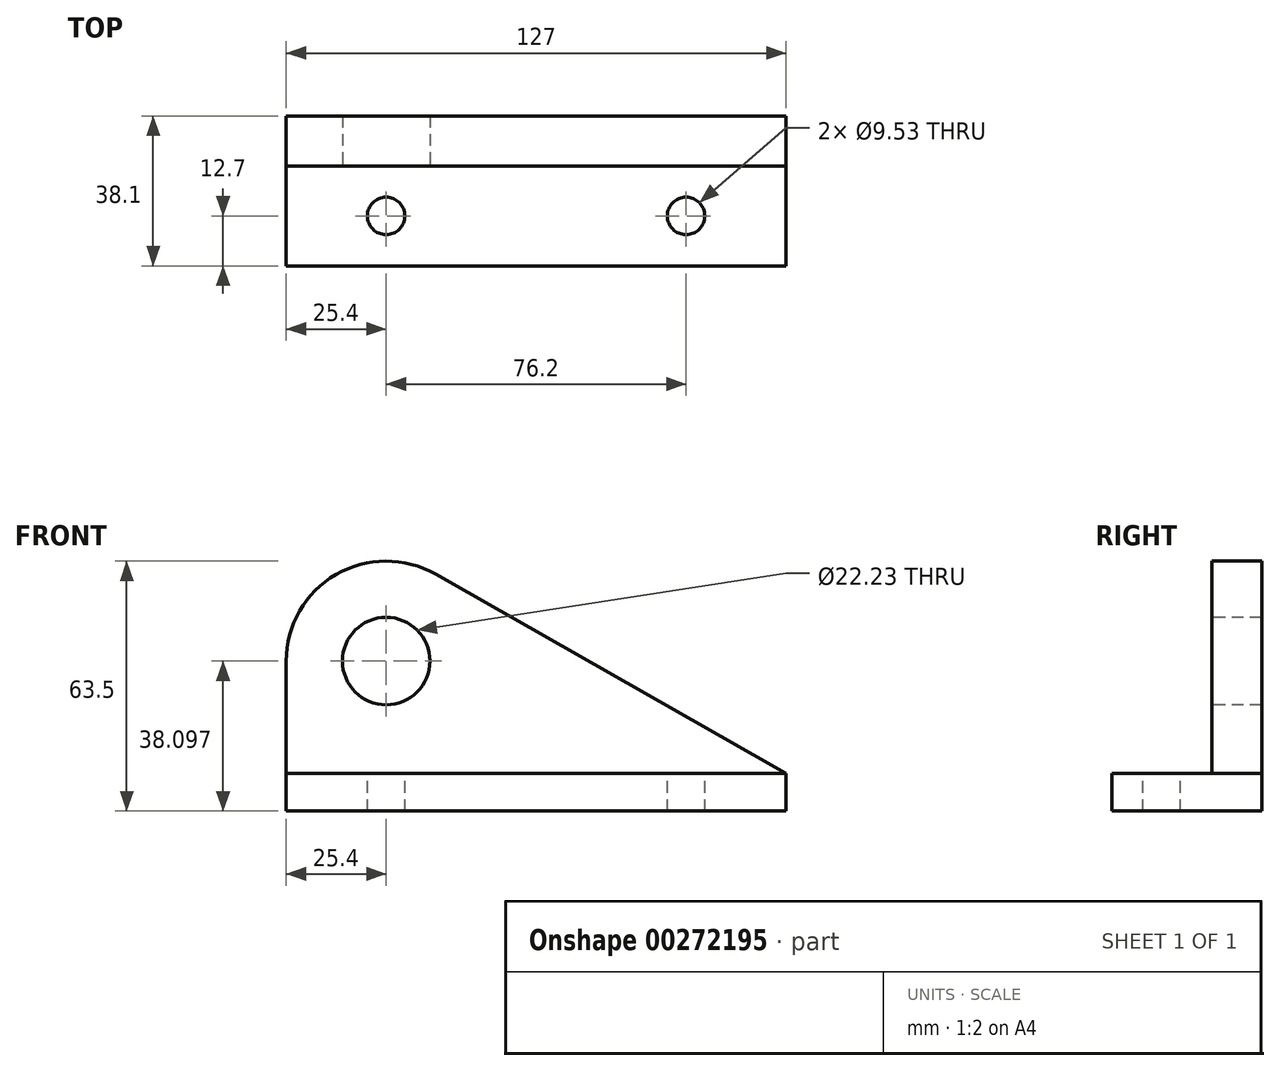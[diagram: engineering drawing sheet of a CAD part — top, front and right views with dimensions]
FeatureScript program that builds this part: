
annotation { "Feature Type Name" : "Feature", "Feature Type Description" : "" }
export const myFeature = defineFeature(function(context is Context, id is Id, definition is map)
    precondition{}
    {
        {
            var Q0;
            Q0=qCreatedBy(makeId("Front.planeOp"),FACE);
            var sketch = newSketch(context, id + "F0", { "sketchPlane" : qUnion([Q0])});
            skLineSegment(sketch, "E0.bottom", {"start": v(-63.5, 4.76) * mm, "end": v(63.5, 4.76) * mm});
            skLineSegment(sketch, "E0.top", {"start": v(-63.5, -4.76) * mm, "end": v(63.5, -4.76) * mm});
            skLineSegment(sketch, "E0.left", {"start": v(-63.5, 4.76) * mm, "end": v(-63.5, -4.76) * mm});
            skLineSegment(sketch, "E0.right", {"start": v(63.5, 4.76) * mm, "end": v(63.5, -4.76) * mm});
            skPoint(sketch, "E0.middle", {"position": v(0, 0) * mm});
            skSolve(sketch);
        }
        {
            var Q0;
            Q0=makeQuery(id+"F0.imprint","IMPRINT",FACE,{"disambiguationData":[TD([[makeQuery(id+"F0.imprint","IMPRINT",EDGE,{"derivedFrom":sQuery(id+"F0.wireOp",EDGE,"E0.bottom")}),-1.0]])]});
            extrude(context, id + "F1", {"entities" : qUnion([Q0]), "endBound" : BoundingType.SYMMETRIC, "depth" : 38.1 * mm});
        }
        {
            var Q0;
            Q0=makeQuery(id+"F1.opExtrude","CAP_FACE",FACE,{"disambiguationData":[OSD([sQuery(id+"F0.wireOp",EDGE,"E0.bottom"),sQuery(id+"F0.wireOp",EDGE,"E0.top"),sQuery(id+"F0.wireOp",EDGE,"E0.left"),sQuery(id+"F0.wireOp",EDGE,"E0.right")])],"isStart":true});
            var sketch = newSketch(context, id + "F2", { "sketchPlane" : qUnion([Q0])});
            skLineSegment(sketch, "E1", {"start": v(63.5, 4.76) * mm, "end": v(38.1, 4.76) * mm});
            skLineSegment(sketch, "E2", {"start": v(31.88, 70.41) * mm, "end": v(36.21, 70.41) * mm});
            skLineSegment(sketch, "E3", {"start": v(38.1, 4.76) * mm, "end": v(38.1, 33.34) * mm});
            skArc(sketch, "E4", {"start": v(63.5, 33.34) * mm, "mid": v(50.87, 55.3) * mm, "end": v(25.54, 55.42) * mm});
            skLineSegment(sketch, "E5", {"start": v(63.5, 4.76) * mm, "end": v(63.5, 33.34) * mm});
            skLineSegment(sketch, "E6", {"start": v(-63.5, 4.76) * mm, "end": v(25.54, 55.42) * mm});
            skSolve(sketch);
        }
        {
            var Q0;
            {var subQ1=sQuery(id+"F2.wireOp",EDGE,"E1");Q0=makeQuery(id+"F2.imprint","IMPRINT",FACE,{"disambiguationData":[TD([[makeQuery(id+"F2.imprint","IMPRINT",EDGE,{"derivedFrom":subQ1}),-1.0]])]});}
            extrude(context, id + "F3", {"entities" : qUnion([Q0]), "operationType" : NewBodyOperationType.ADD, "oppositeDirection" : true, "depth" : 12.7 * mm});
        }
        {
            var Q0;
            Q0=makeQuery(id+"F3.opExtrude","CAP_FACE",FACE,{"disambiguationData":[OSD([sQuery(id+"F0.wireOp",EDGE,"E0.bottom"),sQuery(id+"F2.wireOp",EDGE,"E1"),sQuery(id+"F2.wireOp",EDGE,"E4"),sQuery(id+"F2.wireOp",EDGE,"E5"),sQuery(id+"F2.wireOp",EDGE,"E6")])],"isStart":false});
            var sketch = newSketch(context, id + "F4", { "sketchPlane" : qUnion([Q0])});
            skLineSegment(sketch, "E7", {"start": v(-63.5, 4.76) * mm, "end": v(-38.1, 4.76) * mm});
            skLineSegment(sketch, "E8", {"start": v(-38.1, 4.76) * mm, "end": v(-38.1, 33.34) * mm});
            skSolve(sketch);
        }
        {
            var Q0;
            Q0=sQuery(id+"F4.wireOp",VERTEX,"E8.end");
            var Q1;
            Q1=makeQuery(id+"F1.opExtrude","SWEPT_BODY",BODY,{"disambiguationData":[OSD([sQuery(id+"F0.wireOp",EDGE,"E0.bottom"),sQuery(id+"F0.wireOp",EDGE,"E0.top"),sQuery(id+"F0.wireOp",EDGE,"E0.left"),sQuery(id+"F0.wireOp",EDGE,"E0.right")])]});
            hole(context, id + "F5", {"style" : HoleStyle.SIMPLE, "endStyle" : HoleEndStyle.THROUGH, "holeDiameter" : 22.22 * mm, "tappedDepth" : 12.7 * mm, "tapClearance" : 3, "locations" : qUnion([Q0]), "scope" : qUnion([Q1])});
        }
        {
            var Q0;
            Q0=makeQuery(id+"F1.opExtrude","SWEPT_FACE",FACE,{"disambiguationData":[OSD([sQuery(id+"F0.wireOp",EDGE,"E0.bottom")])]});
            var sketch = newSketch(context, id + "F6", { "sketchPlane" : qUnion([Q0])});
            skLineSegment(sketch, "E9", {"start": v(-63.5, -6.35) * mm, "end": v(-38.1, -6.35) * mm});
            skLineSegment(sketch, "E10", {"start": v(-38.1, -6.35) * mm, "end": v(38.1, -6.35) * mm});
            skSolve(sketch);
        }
        {
            var Q0;
            Q0=sQuery(id+"F6.wireOp",VERTEX,"E10.start");
            var Q1;
            Q1=sQuery(id+"F6.wireOp",VERTEX,"E10.end");
            var Q2;
            Q2=makeQuery(id+"F1.opExtrude","SWEPT_BODY",BODY,{"disambiguationData":[OSD([sQuery(id+"F0.wireOp",EDGE,"E0.bottom"),sQuery(id+"F0.wireOp",EDGE,"E0.top"),sQuery(id+"F0.wireOp",EDGE,"E0.left"),sQuery(id+"F0.wireOp",EDGE,"E0.right")])]});
            hole(context, id + "F7", {"style" : HoleStyle.SIMPLE, "endStyle" : HoleEndStyle.THROUGH, "holeDiameter" : 9.52 * mm, "tappedDepth" : 12.7 * mm, "tapClearance" : 3, "locations" : qUnion([Q0, Q1]), "scope" : qUnion([Q2])});
        }
    });
